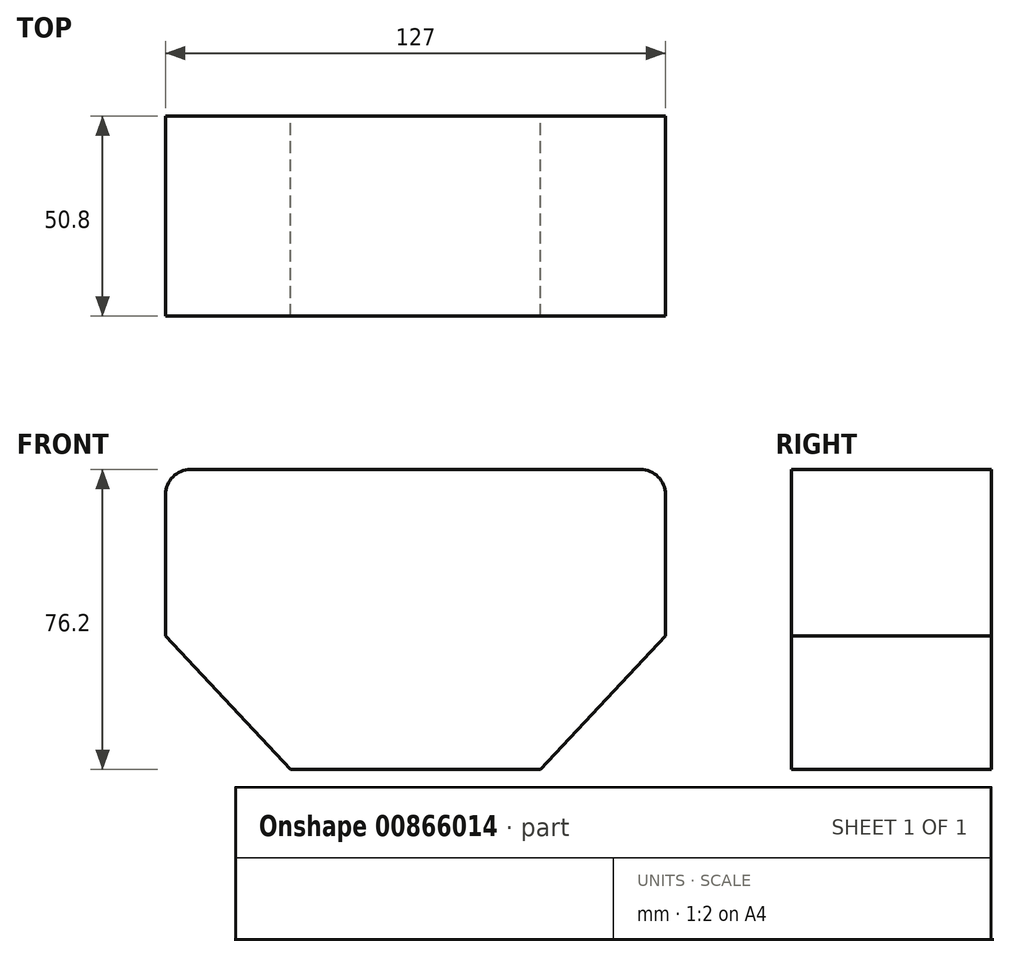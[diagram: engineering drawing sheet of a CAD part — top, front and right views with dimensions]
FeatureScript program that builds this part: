
annotation { "Feature Type Name" : "Feature", "Feature Type Description" : "" }
export const myFeature = defineFeature(function(context is Context, id is Id, definition is map)
    precondition{}
    {
        {
            var Q0;
            Q0=qCreatedBy(makeId("Front.planeOp"),FACE);
            var sketch = newSketch(context, id + "F0", { "sketchPlane" : qUnion([Q0])});
            skLineSegment(sketch, "E0", {"start": v(0, 0) * mm, "end": v(-31.75, 0) * mm});
            skLineSegment(sketch, "E1", {"start": v(-63.5, 33.94) * mm, "end": v(-63.5, 69.85) * mm});
            skLineSegment(sketch, "E2", {"start": v(-57.15, 76.2) * mm, "end": v(0, 76.2) * mm});
            skLineSegment(sketch, "E3.MirrorCS", {"start": v(0, 0) * mm, "end": v(31.75, 0) * mm});
            skLineSegment(sketch, "E4.MirrorCS", {"start": v(63.5, 33.94) * mm, "end": v(63.5, 69.85) * mm});
            skLineSegment(sketch, "E5", {"start": v(0, 76.2) * mm, "end": v(57.15, 76.2) * mm});
            skPoint(sketch, "E6.visualSharp", {"position": v(-63.5, 76.2) * mm});
            skArc(sketch, "E6.filletArc", {"start": v(-57.15, 76.2) * mm, "mid": v(-61.64, 74.34) * mm, "end": v(-63.5, 69.85) * mm});
            skPoint(sketch, "E7.visualSharp", {"position": v(63.5, 76.2) * mm});
            skArc(sketch, "E7.filletArc", {"start": v(63.5, 69.85) * mm, "mid": v(61.64, 74.34) * mm, "end": v(57.15, 76.2) * mm});
            skPoint(sketch, "E8.visualSharp", {"position": v(-63.5, 0) * mm});
            skPoint(sketch, "E9.visualSharp", {"position": v(63.5, 0) * mm});
            skLineSegment(sketch, "E10", {"start": v(-63.5, 33.94) * mm, "end": v(-31.75, 0) * mm});
            skLineSegment(sketch, "E11", {"start": v(31.75, 0) * mm, "end": v(63.5, 33.94) * mm});
            skSolve(sketch);
        }
        {
            var Q0;
            Q0=makeQuery(id+"F0.imprint","IMPRINT",FACE,{"disambiguationData":[TD([[makeQuery(id+"F0.imprint","IMPRINT",EDGE,{"derivedFrom":sQuery(id+"F0.wireOp",EDGE,"E1")}),-1.0]])]});
            extrude(context, id + "F1", {"entities" : qUnion([Q0]), "depth" : 50.8 * mm, "offsetDistance" : 25.4 * mm});
        }
    });
